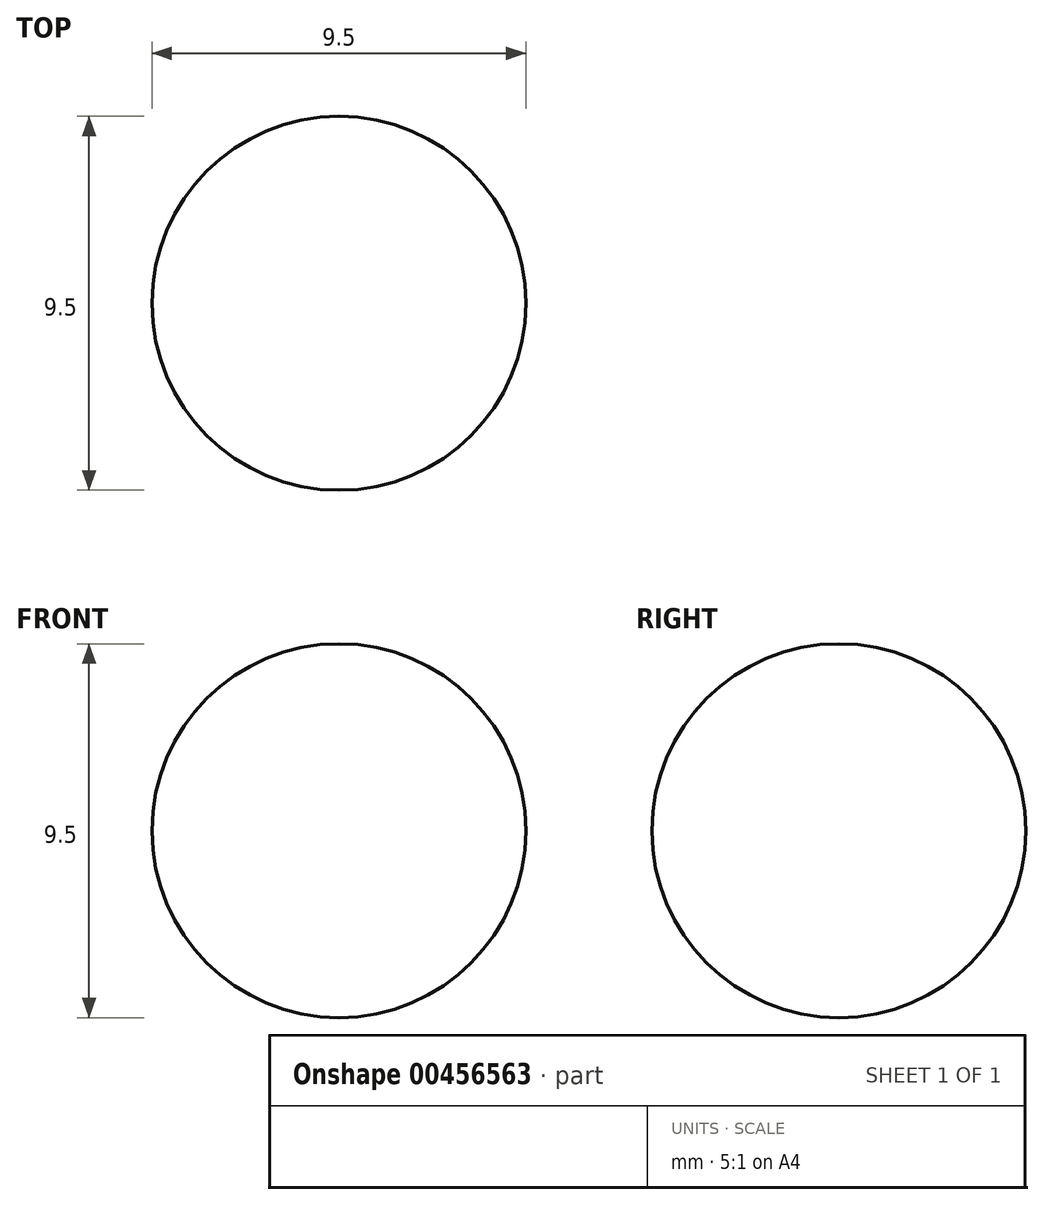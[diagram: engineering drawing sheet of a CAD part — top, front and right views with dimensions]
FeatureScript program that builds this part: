
annotation { "Feature Type Name" : "Feature", "Feature Type Description" : "" }
export const myFeature = defineFeature(function(context is Context, id is Id, definition is map)
    precondition{}
    {
        {
            var Q0;
            Q0=qCreatedBy(makeId("Top.planeOp"),FACE);
            var sketch = newSketch(context, id + "F0", { "sketchPlane" : qUnion([Q0])});
            skArc(sketch, "E0", {"start": v(-4.75, 0) * mm, "mid": v(0, 4.75) * mm, "end": v(4.75, 0) * mm});
            skLineSegment(sketch, "E1", {"start": v(-4.75, 0) * mm, "end": v(4.75, 0) * mm});
            skSolve(sketch);
        }
        {
            var Q0;
            Q0 = qSketchRegion(id + "F0", true);
            var Q1;
            Q1=sQuery(id+"F0.wireOp",EDGE,"E1");
            revolve(context, id + "F1", {"entities" : qUnion([Q0]), "axis" : qUnion([Q1]), "revolveType" : RevolveType.FULL});
        }
    });
